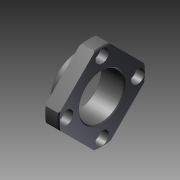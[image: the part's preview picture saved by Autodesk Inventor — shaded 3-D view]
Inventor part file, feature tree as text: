
AUTODESK INVENTOR PART (.ipt)
format: ipt  version: 2016 (Build 200138000, 138)  size: 168,960 bytes
history: native  units: mm
features: other x14, sketch x3, revolve x1, extrude x1, hole x1, pattern_linear x1
ambient origin geometry x8: Origin, YZ Plane, XZ Plane, XY Plane, X Axis, Y Axis, Z Axis, Center Point
bodies: Solid1 (feature_tree)
feature tree (21):
  revolve  "Revolution1"  [1 undecoded]
  extrude  "Extrusion1"  Depth=7.0mm
  hole  "Hole1"  [1 undecoded]
  pattern_linear  "Rectangular Pattern1"  [2 undecoded]
  other  "ff_1_XY"
  other  "ff_1_YZ"
  other  "ff_1_ZX"
  other  "ff_1_X"
  other  "ff_1_Y"
  other  "ff_1_Z"
  other  "ff_1_Center"
  other  "ff_2x_XY"
  other  "ff_2x_YZ"
  other  "ff_2x_ZX"
  other  "ff_2x_X"
  other  "ff_2x_Y"
  other  "ff_2x_Z"
  other  "ff_2x_Center"
  sketch  "Sketch_1"  dims[d0=360.0deg d1=7.0mm d2=0.0mm]
  sketch  "Sketch_2"  dims[d3=3.4mm d4=6.0mm d5=6.5mm d6=4.0mm d7=90.0deg d8=7.0mm d9=0.0mm d10=20.0mm d12=24.748737mm d13=20.0mm d15=24.748737mm]
  sketch  "Sketch3"  dims[d16=0.0mm]
note: 4 required parameter values undecoded (feature->parameter linkage not recoverable at this tier; creation-order binding heuristic only, values carry confidence <= 0.55)